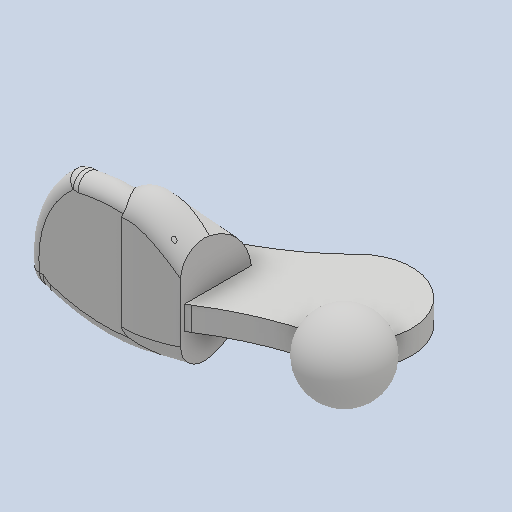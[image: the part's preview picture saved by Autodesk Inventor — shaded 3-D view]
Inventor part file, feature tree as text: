
AUTODESK INVENTOR PART (.ipt)
format: ipt  version: 2025 (Build 290162010, 162A)  size: 452,096 bytes
history: native  units: mm
features: other x10, sketch x5, extrude x3, fillet x2, revolve x1, loft x1
ambient origin geometry x8: Origin, YZ Plane, XZ Plane, XY Plane, X Axis, Y Axis, Z Axis, Center Point
bodies: Body1 (feature_tree), Body2 (feature_tree), Body3 (feature_tree)
feature tree (22):
  other  "Твердое тело1"
  sketch  "Эскиз1"
  sketch  "Эскиз2"
  extrude  "Выдавливание1"  Depth=90.0mm
  revolve  "Вращение1"
  fillet  "Сопряжение1"  Radius=65.0mm
  extrude  "Выдавливание4"  Depth=40.0mm
  other  "РабПлоскость3"
  other  "РабПлоскость4"
  sketch  "Эскиз5"
  sketch  "Эскиз6"
  other  "РабПлоскость5"
  sketch  "Эскиз7"
  extrude  "Выдавливание6"  Depth=70.0mm
  other  "Разделение2"
  fillet  "Сопряжение4"  Radius=95.0mm
  loft  "Лофт5"
  other  "SRF1"
  other  "SRF2"
  other  "Ребра1"
  other  "ВыдавПврх1"
  other  "ВыдавПврх2"
